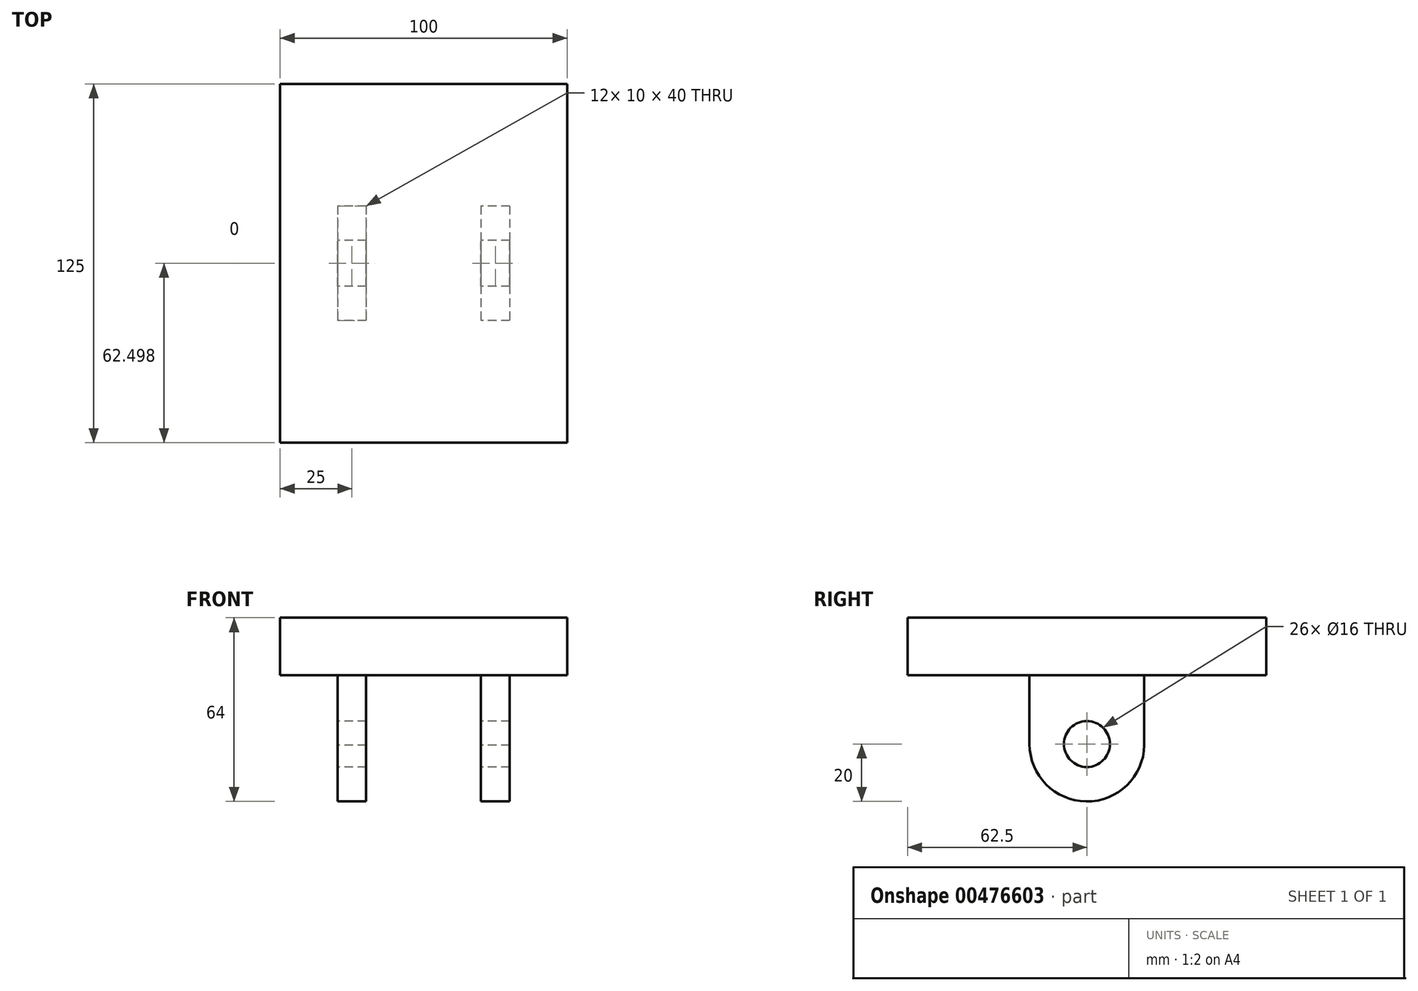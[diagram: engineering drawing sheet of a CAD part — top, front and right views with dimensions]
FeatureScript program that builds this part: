
annotation { "Feature Type Name" : "Feature", "Feature Type Description" : "" }
export const myFeature = defineFeature(function(context is Context, id is Id, definition is map)
    precondition{}
    {
        {
            var Q0;
            Q0=qCreatedBy(makeId("Right.planeOp"),FACE);
            var sketch = newSketch(context, id + "F0", { "sketchPlane" : qUnion([Q0])});
            skLineSegment(sketch, "E0.bottom", {"start": v(-62.5, 10) * mm, "end": v(62.5, 10) * mm});
            skLineSegment(sketch, "E0.top", {"start": v(-62.5, -10) * mm, "end": v(-20, -10) * mm});
            skLineSegment(sketch, "E0.left", {"start": v(-62.5, 10) * mm, "end": v(-62.5, -10) * mm});
            skLineSegment(sketch, "E0.right", {"start": v(62.5, 10) * mm, "end": v(62.5, -10) * mm});
            skPoint(sketch, "E0.middle", {"position": v(0, 0) * mm});
            skArc(sketch, "E1", {"start": v(-20, -33.99) * mm, "mid": v(0.2, -54) * mm, "end": v(20, -33.6) * mm});
            skLineSegment(sketch, "E2", {"start": v(-20, -33.99) * mm, "end": v(-20, -10) * mm});
            skLineSegment(sketch, "E3", {"start": v(20, -34.4) * mm, "end": v(20, -10) * mm});
            skLineSegment(sketch, "E4.trimOffspring", {"start": v(20, -10) * mm, "end": v(62.5, -10) * mm});
            skCircle(sketch, "E5", {"center": v(0, -34) * mm, "radius": 8 * mm});
            skSolve(sketch);
        }
        {
            var Q0;
            Q0=makeQuery(id+"F0.imprint","IMPRINT",FACE,{"disambiguationData":[TD([[makeQuery(id+"F0.imprint","IMPRINT",EDGE,{"derivedFrom":sQuery(id+"F0.wireOp",EDGE,"E0.bottom")}),-1.0]])]});
            extrude(context, id + "F1", {"entities" : qUnion([Q0]), "depth" : 100 * mm});
        }
        {
            var Q0;
            Q0=makeQuery(id+"F1.opExtrude","SWEPT_FACE",FACE,{"disambiguationData":[OSD([sQuery(id+"F0.wireOp",EDGE,"E2")])]});
            var sketch = newSketch(context, id + "F2", { "sketchPlane" : qUnion([Q0])});
            skLineSegment(sketch, "E6.bottom", {"start": v(20, -10) * mm, "end": v(-66.4, -10) * mm});
            skLineSegment(sketch, "E6.top", {"start": v(20, -131.27) * mm, "end": v(-66.4, -131.27) * mm});
            skLineSegment(sketch, "E6.left", {"start": v(20, -10) * mm, "end": v(20, -131.27) * mm});
            skLineSegment(sketch, "E6.right", {"start": v(-66.4, -10) * mm, "end": v(-66.4, -131.27) * mm});
            skLineSegment(sketch, "E7.bottom", {"start": v(80, -10) * mm, "end": v(160.72, -10) * mm});
            skLineSegment(sketch, "E7.top", {"start": v(80, -130.97) * mm, "end": v(160.72, -130.97) * mm});
            skLineSegment(sketch, "E7.left", {"start": v(80, -10) * mm, "end": v(80, -130.97) * mm});
            skLineSegment(sketch, "E7.right", {"start": v(160.72, -10) * mm, "end": v(160.72, -130.97) * mm});
            skLineSegment(sketch, "E8.bottom", {"start": v(30, -10) * mm, "end": v(70, -10) * mm});
            skLineSegment(sketch, "E8.top", {"start": v(30, -136.2) * mm, "end": v(70, -136.2) * mm});
            skLineSegment(sketch, "E8.left", {"start": v(30, -10) * mm, "end": v(30, -136.2) * mm});
            skLineSegment(sketch, "E8.right", {"start": v(70, -10) * mm, "end": v(70, -136.2) * mm});
            skSolve(sketch);
        }
        {
            var Q0;
            {var subQ1=sQuery(id+"F2.wireOp",EDGE,"E6.top");Q0=makeQuery(id+"F2.imprint","IMPRINT",FACE,{"disambiguationData":[TD([[makeQuery(id+"F2.imprint","IMPRINT",EDGE,{"derivedFrom":subQ1}),-1.0]])]});}
            var Q1;
            {var subQ1=sQuery(id+"F0.wireOp",EDGE,"E2");var subQ2=makeQuery(id+"F1.opExtrude","CAP_EDGE",EDGE,{"disambiguationData":[OSD([subQ1])],"isStart":true});Q1=makeQuery(id+"F2.imprint","IMPRINT",FACE,{"disambiguationData":[TD([[makeQuery(id+"F2.imprint","IMPRINT",EDGE,{"derivedFrom":subQ2}),-1.0]])]});}
            var Q2;
            {var subQ0=sQuery(id+"F2.wireOp",EDGE,"E8.bottom");Q2=makeQuery(id+"F2.imprint","IMPRINT",FACE,{"disambiguationData":[TD([[makeQuery(id+"F2.imprint","IMPRINT",EDGE,{"derivedFrom":subQ0}),1.0]])]});}
            var Q3;
            {var subQ0=sQuery(id+"F2.wireOp",EDGE,"E8.top");Q3=makeQuery(id+"F2.imprint","IMPRINT",FACE,{"disambiguationData":[TD([[makeQuery(id+"F2.imprint","IMPRINT",EDGE,{"derivedFrom":subQ0}),1.0]])]});}
            var Q4;
            {var subQ1=sQuery(id+"F2.wireOp",EDGE,"E7.top");Q4=makeQuery(id+"F2.imprint","IMPRINT",FACE,{"disambiguationData":[TD([[makeQuery(id+"F2.imprint","IMPRINT",EDGE,{"derivedFrom":subQ1}),1.0]])]});}
            var Q5;
            {var subQ1=sQuery(id+"F0.wireOp",EDGE,"E2");var subQ2=makeQuery(id+"F1.opExtrude","CAP_EDGE",EDGE,{"disambiguationData":[OSD([subQ1])],"isStart":false});Q5=makeQuery(id+"F2.imprint","IMPRINT",FACE,{"disambiguationData":[TD([[makeQuery(id+"F2.imprint","IMPRINT",EDGE,{"derivedFrom":subQ2}),1.0]])]});}
            extrude(context, id + "F3", {"entities" : qUnion([Q0, Q1, Q2, Q3, Q4, Q5]), "operationType" : NewBodyOperationType.REMOVE, "endBound" : BoundingType.THROUGH_ALL, "oppositeDirection" : true, "depth" : 25 * mm});
        }
    });
